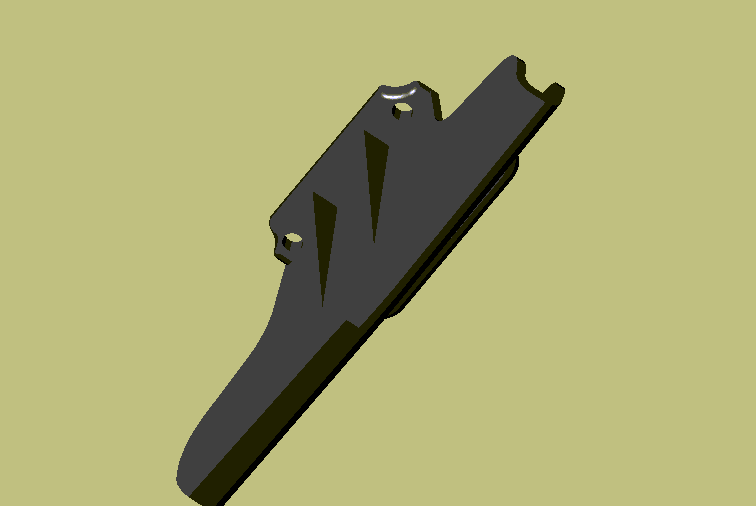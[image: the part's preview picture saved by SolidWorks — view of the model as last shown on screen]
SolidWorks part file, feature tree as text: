
SOLIDWORKS PART (.sldprt)
format: sldprt  version: not decoded by parser v0  size: 282,624 bytes
history: native  units: mm
features: sketch x6, fillet x5, cut_extrude x4, plane x3, extrude x2, material x1 (+8 scaffold rows collapsed)
feature tree (29):
  scaffold x8  (default folders/planes/origin — collapsed)
  material  "Matériau <non spécifié>"
  plane  "Plane1"
  plane  "Plane2"
  plane  "Plane3"
  sketch  "Esquisse1"  dims[D5=80.0mm D6=8.0mm D1=50.0mm D2=37.0mm D3=42.0mm D4=4.0mm]
  extrude  "Base-Extrusion"  Depth=27mm
  sketch  "Esquisse2"  dims[D1=13.5mm D2=13.0mm D3=8.0mm D4=6.0mm]
  cut_extrude  "Enlèv. mat.-Extru.1"  Depth=273mm
  fillet  "Congé3"  Radius=3mm
  fillet  "Congé5"  Radius=2mm
  fillet  "Congé6"  Radius=5mm
  fillet  "Congé7"  Radius=2mm
  sketch  "Esquisse5"  dims[D1=3.5mm D2=32.1975mm D3=17.0mm]
  cut_extrude  "Enlèv. mat.-Extru.6"  [1 undecoded]
  sketch  "Esquisse7"  dims[c1.D1=~28.417608mm c2.D1=4.0deg c2.D2=~28.417608mm c3.D2=175.0deg c4.D2=~28.417608mm c5.D2=4.0deg]
  extrude  "Boss.-Extru.1"  Depth=5mm
  sketch  "Esquisse10"
  cut_extrude  "Enlèv. mat.-Extru.8"  Depth=105mm
  sketch  "Esquisse11"  dims[D3=10.0mm D1=1.0mm D2=43.0mm]
  cut_extrude  "Enlèv. mat.-Extru.9"  Depth=10mm
  fillet  "Congé9"  Radius=1mm
decode coverage: 15 of 17 modeling features carry decoded parameters
note: ~ marks probable driven/reference dimensions
note: 1 parameter value undecoded
note: suppression state not decoded; provenance and decode notes live in map.json
